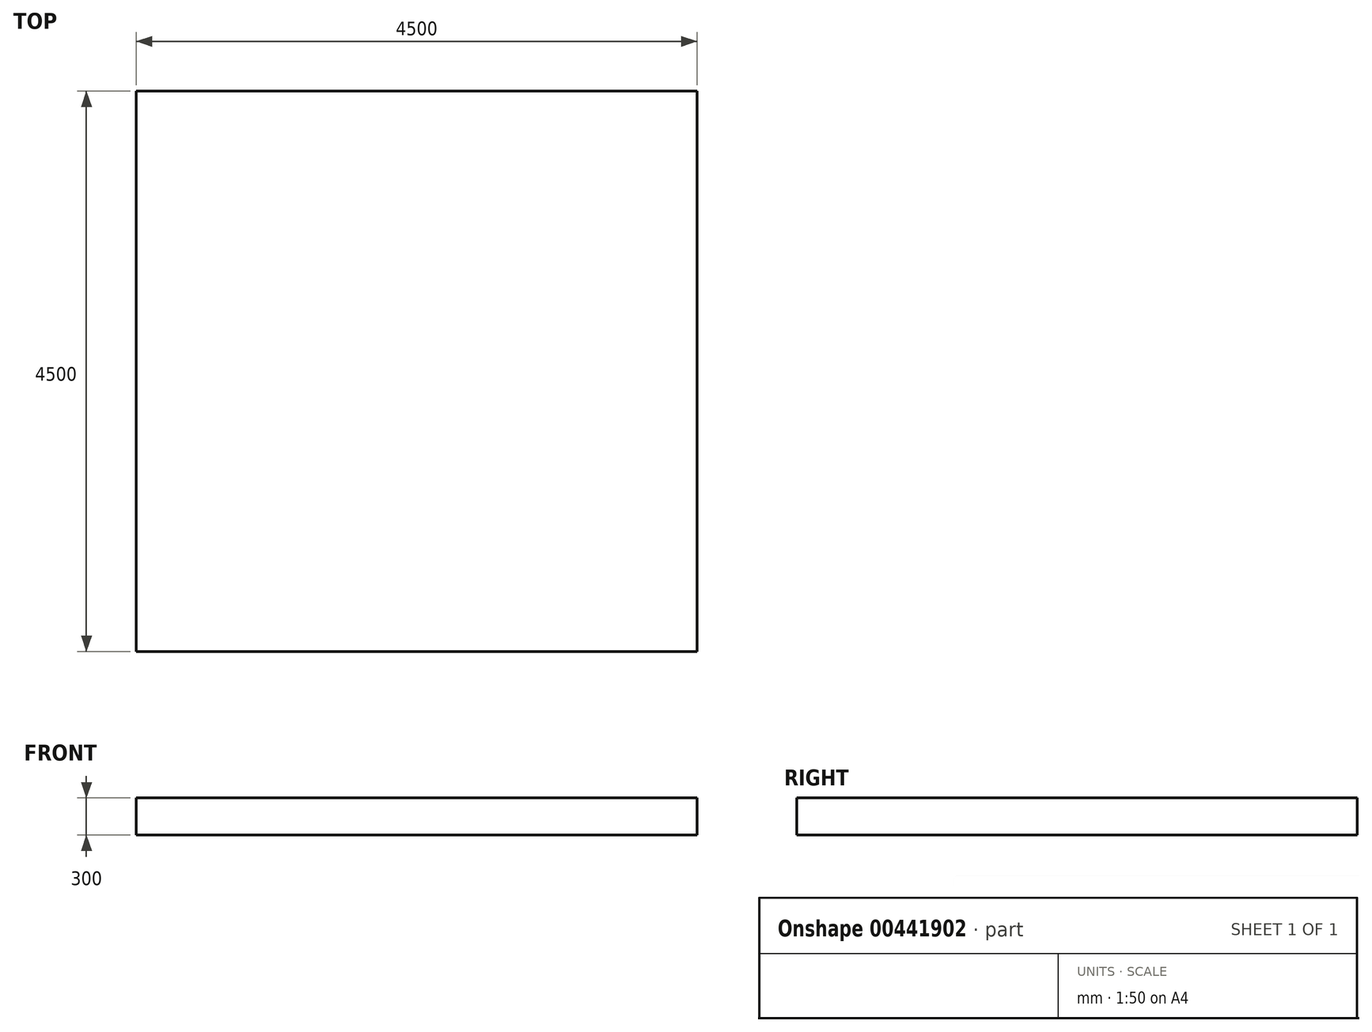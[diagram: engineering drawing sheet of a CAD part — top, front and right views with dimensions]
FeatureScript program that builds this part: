
annotation { "Feature Type Name" : "Feature", "Feature Type Description" : "" }
export const myFeature = defineFeature(function(context is Context, id is Id, definition is map)
    precondition{}
    {
        {
            var Q0;
            Q0=qCreatedBy(makeId("Top.planeOp"),FACE);
            var sketch = newSketch(context, id + "F0", { "sketchPlane" : qUnion([Q0])});
            skLineSegment(sketch, "E0.bottom", {"start": v(-2250, -2250) * mm, "end": v(2250, -2250) * mm});
            skLineSegment(sketch, "E0.top", {"start": v(-2250, 2250) * mm, "end": v(2250, 2250) * mm});
            skLineSegment(sketch, "E0.left", {"start": v(-2250, -2250) * mm, "end": v(-2250, 2250) * mm});
            skLineSegment(sketch, "E0.right", {"start": v(2250, -2250) * mm, "end": v(2250, 2250) * mm});
            skPoint(sketch, "E0.middle", {"position": v(0, 0) * mm});
            skSolve(sketch);
        }
        {
            var Q0;
            Q0=makeQuery(id+"F0.imprint","IMPRINT",FACE,{"disambiguationData":[TD([[makeQuery(id+"F0.imprint","IMPRINT",EDGE,{"derivedFrom":sQuery(id+"F0.wireOp",EDGE,"E0.bottom")}),1.0]])]});
            extrude(context, id + "F1", {"entities" : qUnion([Q0]), "oppositeDirection" : true, "depth" : 300 * mm});
        }
    });
